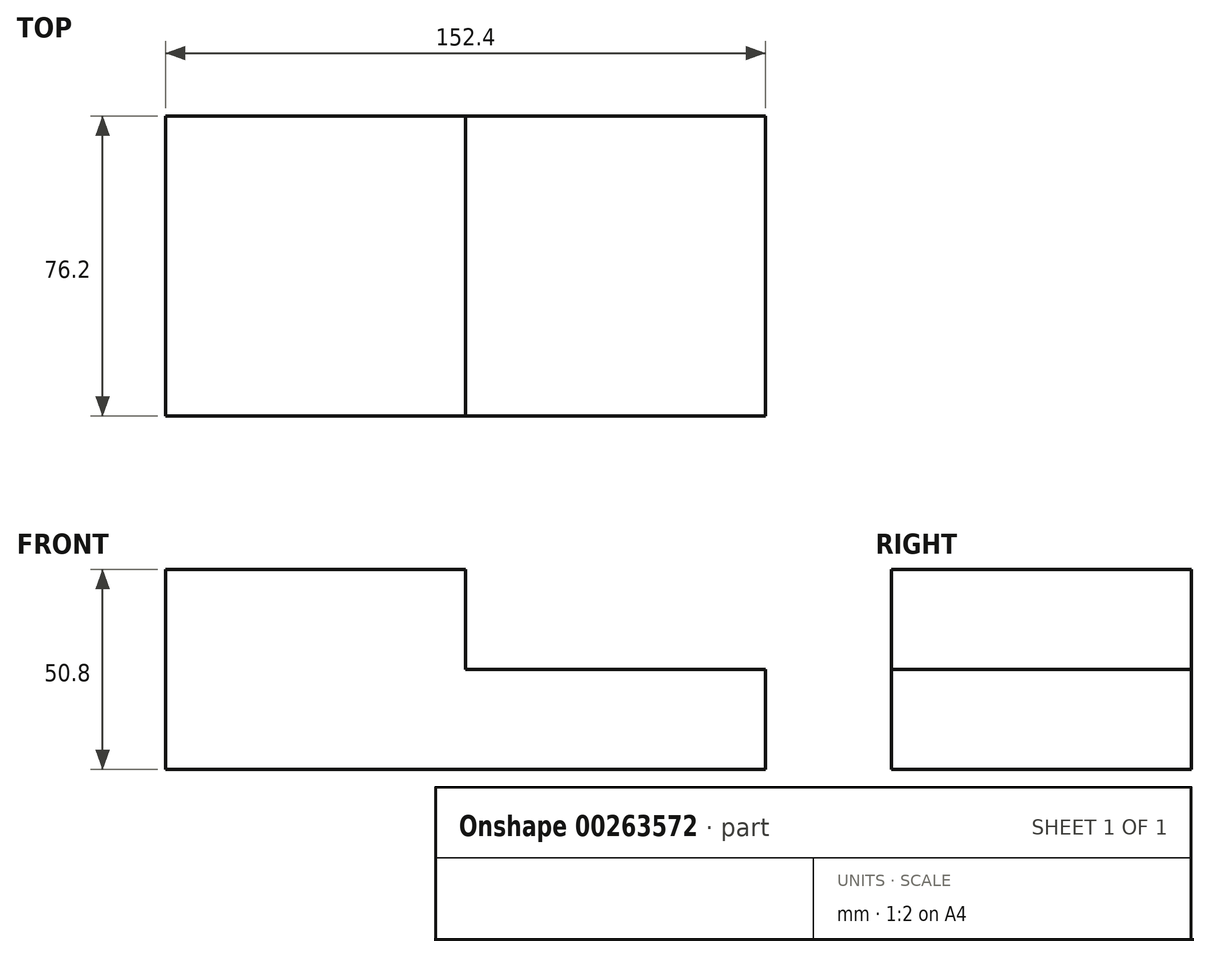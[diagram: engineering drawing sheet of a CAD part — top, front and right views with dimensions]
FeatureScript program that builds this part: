
annotation { "Feature Type Name" : "Feature", "Feature Type Description" : "" }
export const myFeature = defineFeature(function(context is Context, id is Id, definition is map)
    precondition{}
    {
        {
            var Q0;
            Q0=qCreatedBy(makeId("Front.planeOp"),FACE);
            var sketch = newSketch(context, id + "F0", { "sketchPlane" : qUnion([Q0])});
            skLineSegment(sketch, "E0.bottom", {"start": v(-76.2, 35.64) * mm, "end": v(0, 35.64) * mm});
            skLineSegment(sketch, "E0.left", {"start": v(-76.2, 35.64) * mm, "end": v(-76.2, -15.16) * mm});
            skLineSegment(sketch, "E0.right", {"start": v(0, 35.64) * mm, "end": v(0, 10.24) * mm});
            skLineSegment(sketch, "E1.bottom", {"start": v(0, 10.24) * mm, "end": v(76.2, 10.24) * mm});
            skLineSegment(sketch, "E1.right", {"start": v(76.2, 10.24) * mm, "end": v(76.2, -15.16) * mm});
            skPoint(sketch, "E0.top.end.orphan", {"position": v(0, -15.16) * mm});
            skLineSegment(sketch, "E2", {"start": v(-76.2, -15.16) * mm, "end": v(76.2, -15.16) * mm});
            skSolve(sketch);
        }
        {
            var Q0;
            Q0 = qSketchRegion(id + "F0", true);
            extrude(context, id + "F1", {"entities" : qUnion([Q0]), "depth" : 76.2 * mm});
        }
    });
